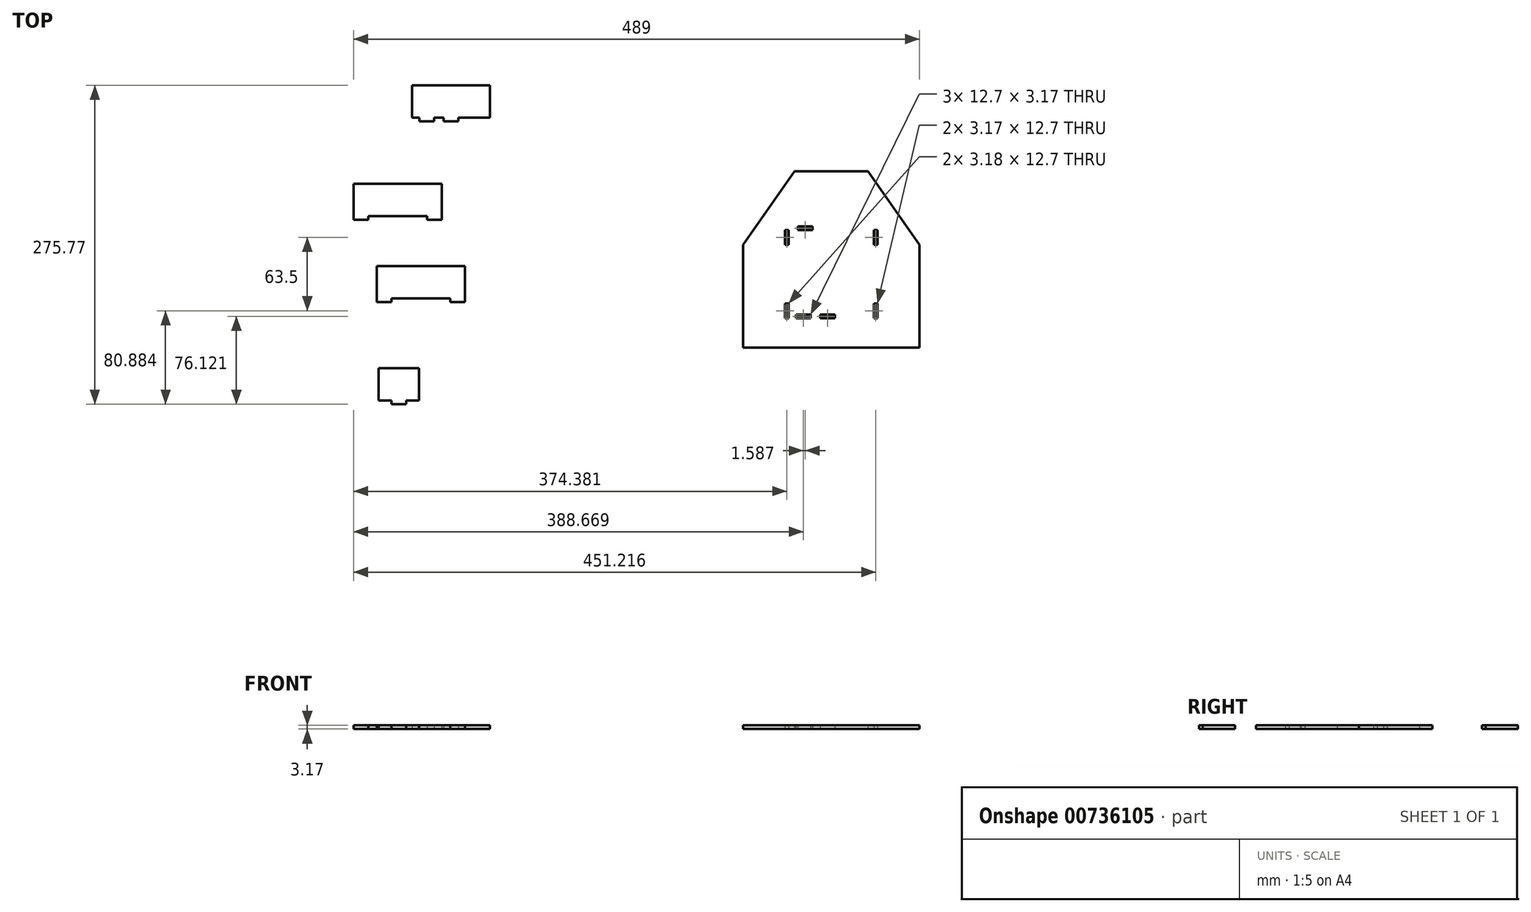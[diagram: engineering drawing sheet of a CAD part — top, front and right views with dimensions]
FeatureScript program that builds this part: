
annotation { "Feature Type Name" : "Feature", "Feature Type Description" : "" }
export const myFeature = defineFeature(function(context is Context, id is Id, definition is map)
    precondition{}
    {
        {
            var Q0;
            Q0=qCreatedBy(makeId("Top.planeOp"),FACE);
            var sketch = newSketch(context, id + "F0", { "sketchPlane" : qUnion([Q0])});
            skLineSegment(sketch, "E0", {"start": v(-54.28, -110.33) * mm, "end": v(98.12, -110.33) * mm});
            skLineSegment(sketch, "E1", {"start": v(-54.28, -110.33) * mm, "end": v(-54.28, -21.43) * mm});
            skLineSegment(sketch, "E2", {"start": v(-54.28, -21.43) * mm, "end": v(-9.83, 42.07) * mm});
            skLineSegment(sketch, "E3", {"start": v(98.12, -110.33) * mm, "end": v(98.12, -21.43) * mm});
            skLineSegment(sketch, "E4", {"start": v(53.67, 42.07) * mm, "end": v(98.12, -21.43) * mm});
            skLineSegment(sketch, "E5", {"start": v(-54.28, -110.33) * mm, "end": v(-41.58, -110.33) * mm});
            skLineSegment(sketch, "E6", {"start": v(98.12, -110.33) * mm, "end": v(85.42, -110.33) * mm});
            skLineSegment(sketch, "E7", {"start": v(98.12, -110.33) * mm, "end": v(98.12, -98) * mm});
            skLineSegment(sketch, "E8", {"start": v(-54.28, -110.33) * mm, "end": v(-18.09, -110.33) * mm});
            skLineSegment(sketch, "E9", {"start": v(98.12, -110.33) * mm, "end": v(53.67, -110.33) * mm});
            skLineSegment(sketch, "E10", {"start": v(-54.28, -110.33) * mm, "end": v(-54.28, -26.5) * mm});
            skLineSegment(sketch, "E11", {"start": v(98.12, -110.33) * mm, "end": v(98.12, -34.13) * mm});
            skLineSegment(sketch, "E12", {"start": v(98.12, -110.33) * mm, "end": v(98.12, -26.5) * mm});
            skLineSegment(sketch, "E13", {"start": v(-54.28, -110.33) * mm, "end": v(0, -110.33) * mm});
            skLineSegment(sketch, "E14", {"start": v(-54.28, -110.33) * mm, "end": v(21.92, -110.33) * mm});
            skLineSegment(sketch, "E15.bottom", {"start": v(-18.09, -84.93) * mm, "end": v(-14.91, -84.93) * mm});
            skLineSegment(sketch, "E15.top", {"start": v(-18.09, -72.23) * mm, "end": v(-14.91, -72.23) * mm});
            skLineSegment(sketch, "E15.left", {"start": v(-18.09, -84.93) * mm, "end": v(-18.09, -72.23) * mm});
            skLineSegment(sketch, "E15.right", {"start": v(-14.91, -84.93) * mm, "end": v(-14.91, -72.23) * mm});
            skLineSegment(sketch, "E16", {"start": v(-18.09, -21.43) * mm, "end": v(-18.09, -8.73) * mm});
            skLineSegment(sketch, "E17", {"start": v(-18.09, -8.73) * mm, "end": v(-14.91, -8.73) * mm});
            skLineSegment(sketch, "E18", {"start": v(-14.91, -8.73) * mm, "end": v(-14.91, -21.43) * mm});
            skLineSegment(sketch, "E19", {"start": v(-14.91, -21.43) * mm, "end": v(-18.09, -21.43) * mm});
            skLineSegment(sketch, "E20.MirrorCS", {"start": v(58.75, -8.73) * mm, "end": v(58.75, -21.43) * mm});
            skLineSegment(sketch, "E21.MirrorCS", {"start": v(61.92, -8.73) * mm, "end": v(58.75, -8.73) * mm});
            skLineSegment(sketch, "E22.MirrorCS", {"start": v(58.75, -21.43) * mm, "end": v(61.92, -21.43) * mm});
            skLineSegment(sketch, "E23.MirrorCS", {"start": v(61.92, -21.43) * mm, "end": v(61.92, -8.73) * mm});
            skLineSegment(sketch, "E24.MirrorCS", {"start": v(58.75, -84.93) * mm, "end": v(58.75, -72.23) * mm});
            skLineSegment(sketch, "E25.MirrorCS", {"start": v(61.92, -84.93) * mm, "end": v(61.92, -72.23) * mm});
            skLineSegment(sketch, "E26.MirrorCS", {"start": v(61.92, -84.93) * mm, "end": v(58.75, -84.93) * mm});
            skLineSegment(sketch, "E27.MirrorCS", {"start": v(61.92, -72.23) * mm, "end": v(58.75, -72.23) * mm});
            skLineSegment(sketch, "E28", {"start": v(-9.83, 42.07) * mm, "end": v(54.4, 42.07) * mm});
            skLineSegment(sketch, "E29", {"start": v(-0.62, -8.73) * mm, "end": v(-6.97, -8.73) * mm});
            skLineSegment(sketch, "E30", {"start": v(-0.62, -8.73) * mm, "end": v(5.73, -8.73) * mm});
            skLineSegment(sketch, "E31.bottom", {"start": v(-6.97, -8.73) * mm, "end": v(5.73, -8.73) * mm});
            skLineSegment(sketch, "E31.top", {"start": v(-6.97, -5.55) * mm, "end": v(5.73, -5.55) * mm});
            skLineSegment(sketch, "E31.left", {"start": v(-6.97, -8.73) * mm, "end": v(-6.97, -5.55) * mm});
            skLineSegment(sketch, "E31.right", {"start": v(5.73, -8.73) * mm, "end": v(5.73, -5.55) * mm});
            skLineSegment(sketch, "E32", {"start": v(18.74, -84.93) * mm, "end": v(12.4, -84.93) * mm});
            skLineSegment(sketch, "E33.bottom", {"start": v(12.4, -84.93) * mm, "end": v(25.1, -84.93) * mm});
            skLineSegment(sketch, "E33.top", {"start": v(12.4, -81.75) * mm, "end": v(25.1, -81.75) * mm});
            skLineSegment(sketch, "E33.left", {"start": v(12.4, -84.93) * mm, "end": v(12.4, -81.75) * mm});
            skLineSegment(sketch, "E33.right", {"start": v(25.1, -84.93) * mm, "end": v(25.1, -81.75) * mm});
            skLineSegment(sketch, "E34", {"start": v(-2.21, -84.93) * mm, "end": v(4.14, -84.93) * mm});
            skLineSegment(sketch, "E35.bottom", {"start": v(4.14, -84.93) * mm, "end": v(-8.56, -84.93) * mm});
            skLineSegment(sketch, "E35.top", {"start": v(4.14, -81.75) * mm, "end": v(-8.56, -81.75) * mm});
            skLineSegment(sketch, "E35.left", {"start": v(4.14, -84.93) * mm, "end": v(4.14, -81.75) * mm});
            skLineSegment(sketch, "E35.right", {"start": v(-8.56, -84.93) * mm, "end": v(-8.56, -81.75) * mm});
            skSolve(sketch);
        }
        {
            var Q0;
            Q0=qCreatedBy(makeId("Top.planeOp"),FACE);
            var sketch = newSketch(context, id + "F1", { "sketchPlane" : qUnion([Q0])});
            skLineSegment(sketch, "E36.bottom", {"start": v(-340.37, 116.31) * mm, "end": v(-273.06, 116.31) * mm});
            skLineSegment(sketch, "E36.left", {"start": v(-340.37, 116.31) * mm, "end": v(-340.37, 88.37) * mm});
            skLineSegment(sketch, "E36.right", {"start": v(-273.06, 116.31) * mm, "end": v(-273.06, 88.37) * mm});
            skLineSegment(sketch, "E37.bottom", {"start": v(-390.88, 31.12) * mm, "end": v(-314.68, 31.12) * mm});
            skLineSegment(sketch, "E37.left", {"start": v(-390.88, 31.12) * mm, "end": v(-390.88, 3.18) * mm});
            skLineSegment(sketch, "E37.right", {"start": v(-314.68, 31.12) * mm, "end": v(-314.68, 3.18) * mm});
            skLineSegment(sketch, "E38.bottom", {"start": v(-370.87, -39.96) * mm, "end": v(-294.67, -39.96) * mm});
            skLineSegment(sketch, "E38.left", {"start": v(-370.87, -39.96) * mm, "end": v(-370.87, -67.9) * mm});
            skLineSegment(sketch, "E38.right", {"start": v(-294.67, -39.96) * mm, "end": v(-294.67, -67.9) * mm});
            skLineSegment(sketch, "E39.bottom", {"start": v(-369.15, -128.35) * mm, "end": v(-334.22, -128.35) * mm});
            skLineSegment(sketch, "E39.left", {"start": v(-369.15, -128.35) * mm, "end": v(-369.15, -156.29) * mm});
            skLineSegment(sketch, "E39.right", {"start": v(-334.22, -128.35) * mm, "end": v(-334.22, -156.29) * mm});
            skLineSegment(sketch, "E40.top", {"start": v(-314.68, 0) * mm, "end": v(-327.38, 0) * mm});
            skLineSegment(sketch, "E40.left", {"start": v(-314.68, 3.18) * mm, "end": v(-314.68, 0) * mm});
            skLineSegment(sketch, "E40.right", {"start": v(-327.38, 3.18) * mm, "end": v(-327.38, 0) * mm});
            skLineSegment(sketch, "E41.top", {"start": v(-390.88, 0) * mm, "end": v(-378.18, 0) * mm});
            skLineSegment(sketch, "E41.left", {"start": v(-390.88, 3.18) * mm, "end": v(-390.88, 0) * mm});
            skLineSegment(sketch, "E41.right", {"start": v(-378.18, 3.18) * mm, "end": v(-378.18, 0) * mm});
            skLineSegment(sketch, "E42.top", {"start": v(-294.67, -71.07) * mm, "end": v(-307.37, -71.07) * mm});
            skLineSegment(sketch, "E42.left", {"start": v(-294.67, -67.9) * mm, "end": v(-294.67, -71.07) * mm});
            skLineSegment(sketch, "E42.right", {"start": v(-307.37, -67.9) * mm, "end": v(-307.37, -71.07) * mm});
            skLineSegment(sketch, "E43.top", {"start": v(-370.87, -71.07) * mm, "end": v(-358.17, -71.07) * mm});
            skLineSegment(sketch, "E43.left", {"start": v(-370.87, -67.9) * mm, "end": v(-370.87, -71.07) * mm});
            skLineSegment(sketch, "E43.right", {"start": v(-358.17, -67.9) * mm, "end": v(-358.17, -71.07) * mm});
            skLineSegment(sketch, "E44.top", {"start": v(-358.03, -159.46) * mm, "end": v(-345.33, -159.46) * mm});
            skLineSegment(sketch, "E44.left", {"start": v(-358.03, -156.29) * mm, "end": v(-358.03, -159.46) * mm});
            skLineSegment(sketch, "E44.right", {"start": v(-345.33, -156.29) * mm, "end": v(-345.33, -159.46) * mm});
            skLineSegment(sketch, "E45", {"start": v(-340.37, 88.37) * mm, "end": v(-334.02, 88.37) * mm});
            skLineSegment(sketch, "E46.top", {"start": v(-334.02, 85.2) * mm, "end": v(-321.32, 85.2) * mm});
            skLineSegment(sketch, "E46.left", {"start": v(-334.02, 88.37) * mm, "end": v(-334.02, 85.2) * mm});
            skLineSegment(sketch, "E46.right", {"start": v(-321.32, 88.37) * mm, "end": v(-321.32, 85.2) * mm});
            skLineSegment(sketch, "E47", {"start": v(-321.32, 88.37) * mm, "end": v(-313.06, 88.37) * mm});
            skLineSegment(sketch, "E48.top", {"start": v(-313.06, 85.2) * mm, "end": v(-300.36, 85.2) * mm});
            skLineSegment(sketch, "E48.left", {"start": v(-313.06, 88.37) * mm, "end": v(-313.06, 85.2) * mm});
            skLineSegment(sketch, "E48.right", {"start": v(-300.36, 88.37) * mm, "end": v(-300.36, 85.2) * mm});
            skLineSegment(sketch, "E49", {"start": v(-273.06, 88.37) * mm, "end": v(-300.36, 88.37) * mm});
            skLineSegment(sketch, "E50", {"start": v(-378.18, 3.18) * mm, "end": v(-327.38, 3.18) * mm});
            skLineSegment(sketch, "E51", {"start": v(-358.17, -67.9) * mm, "end": v(-307.37, -67.9) * mm});
            skLineSegment(sketch, "E52", {"start": v(-369.15, -156.29) * mm, "end": v(-358.03, -156.29) * mm});
            skLineSegment(sketch, "E53", {"start": v(-345.33, -156.29) * mm, "end": v(-334.22, -156.29) * mm});
            skSolve(sketch);
        }
        {
            var Q0;
            Q0=makeQuery(id+"F1.imprint","IMPRINT",FACE,{"disambiguationData":[TD([[makeQuery(id+"F1.imprint","IMPRINT",EDGE,{"derivedFrom":sQuery(id+"F1.wireOp",EDGE,"E36.bottom")}),-1.0]])]});
            var Q1;
            Q1=makeQuery(id+"F1.imprint","IMPRINT",FACE,{"disambiguationData":[TD([[makeQuery(id+"F1.imprint","IMPRINT",EDGE,{"derivedFrom":sQuery(id+"F1.wireOp",EDGE,"E37.bottom")}),-1.0]])]});
            var Q2;
            Q2=makeQuery(id+"F1.imprint","IMPRINT",FACE,{"disambiguationData":[TD([[makeQuery(id+"F1.imprint","IMPRINT",EDGE,{"derivedFrom":sQuery(id+"F1.wireOp",EDGE,"E38.bottom")}),-1.0]])]});
            var Q3;
            Q3=makeQuery(id+"F1.imprint","IMPRINT",FACE,{"disambiguationData":[TD([[makeQuery(id+"F1.imprint","IMPRINT",EDGE,{"derivedFrom":sQuery(id+"F1.wireOp",EDGE,"E39.bottom")}),-1.0]])]});
            var Q4;
            Q4=makeQuery(id+"F1.imprint","IMPRINT",FACE,{"disambiguationData":[TD([[makeQuery(id+"F1.imprint","IMPRINT",EDGE,{"derivedFrom":sQuery(id+"F1.wireOp",EDGE,"0buRZNJO-JQhi-fAal-7aa5-5hUd0YiLziv1.bottom")}),-1.0]])]});
            extrude(context, id + "F2", {"entities" : qUnion([Q0, Q1, Q2, Q3, Q4]), "depth" : 3.17 * mm, "offsetDistance" : 25.4 * mm});
        }
        {
            var Q0;
            Q0=makeQuery(id+"F0.imprint","IMPRINT",FACE,{"disambiguationData":[TD([[makeQuery(id+"F0.imprint","IMPRINT",EDGE,{"derivedFrom":sQuery(id+"F0.wireOp",EDGE,"1OJ5z02J-0AuK-m2Yd-ZkWO-OHtXmqfcO3yS.top")}),1.0]])]});
            var Q1;
            {var subQ2=sQuery(id+"F0.wireOp",EDGE,"E0");Q1=makeQuery(id+"F0.imprint","IMPRINT",FACE,{"disambiguationData":[TD([[makeQuery(id+"F0.imprint","IMPRINT",EDGE,{"derivedFrom":subQ2}),1.0]])]});}
            extrude(context, id + "F3", {"entities" : qUnion([Q0, Q1]), "depth" : 3.17 * mm, "offsetDistance" : 25.4 * mm});
        }
    });
